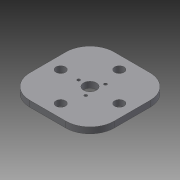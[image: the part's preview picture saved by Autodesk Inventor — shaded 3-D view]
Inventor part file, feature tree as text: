
AUTODESK INVENTOR PART (.ipt)
format: ipt  version: 2015 (Build 190159000, 159)  size: 116,736 bytes
history: native  units: in
note: dims shown in document units (in); Inventor stores cm internally (conversion verified against a paired STEP export)
features: extrude x1, fillet x1, sketch x1
ambient origin geometry x8: Origin, YZ Plane, XZ Plane, XY Plane, X Axis, Y Axis, Z Axis, Center Point
bodies: Body1 (feature_tree)
feature tree (3):
  extrude  "Extrusion6"  TaperAngle=120.0deg  [1 undecoded]
  fillet  "Fillet1"  Radius=0.4734in
  sketch  "Sketch3"  dims[d19=120.0deg d20=120.0deg d21=0.4734in d22=0.4734in d23=0.4734in d24=0.1174in d25=0.1174in d26=0.1174in d27=2.4409in d28=2.4409in d29=0.3937in d30=0.3937in d31=3.5in d32=3.5in d33=0.25in d34=0.0in d35=1.0in]
note: 1 required parameter value undecoded (feature->parameter linkage not recoverable at this tier; creation-order binding heuristic only, values carry confidence <= 0.55)
